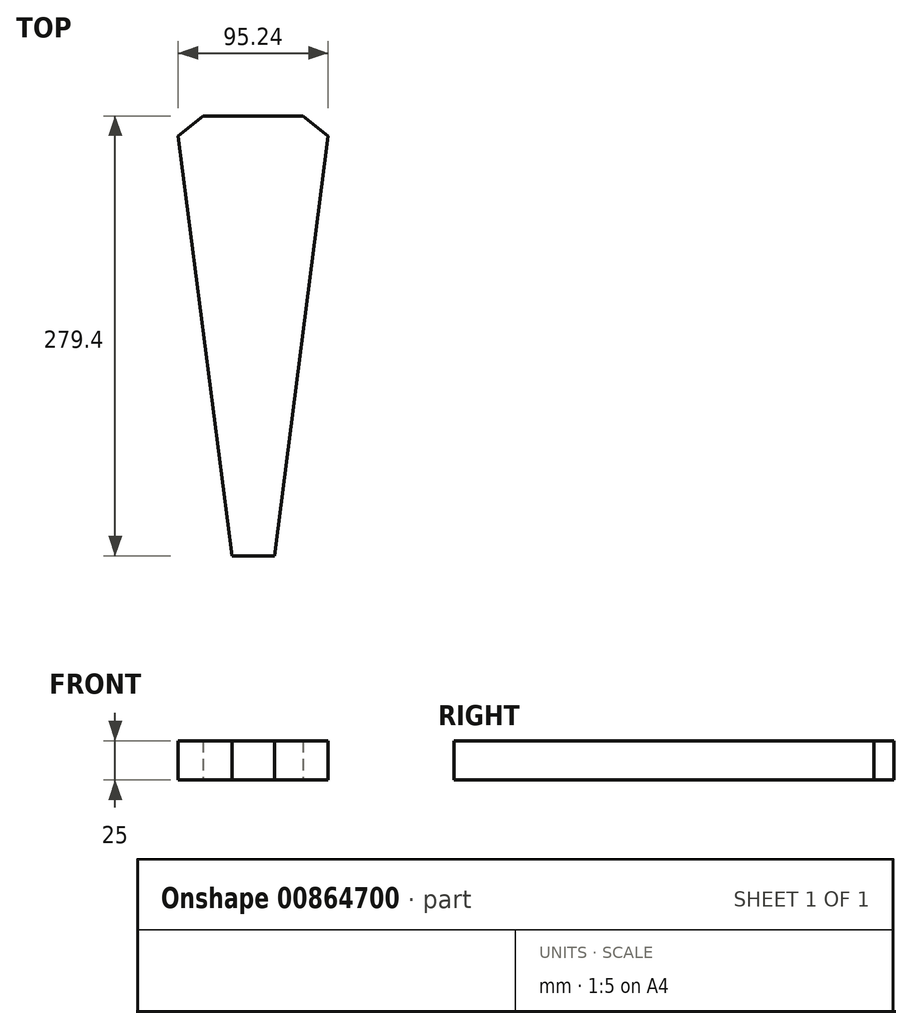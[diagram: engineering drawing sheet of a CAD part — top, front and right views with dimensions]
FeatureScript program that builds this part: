
annotation { "Feature Type Name" : "Feature", "Feature Type Description" : "" }
export const myFeature = defineFeature(function(context is Context, id is Id, definition is map)
    precondition{}
    {
        {
            var Q0;
            Q0=qCreatedBy(makeId("Top.planeOp"),FACE);
            var sketch = newSketch(context, id + "F0", { "sketchPlane" : qUnion([Q0])});
            skLineSegment(sketch, "E0.bottom", {"start": v(47.63, 139.7) * mm, "end": v(-47.62, 139.7) * mm, "construction": true});
            skLineSegment(sketch, "E0.top", {"start": v(47.62, -139.7) * mm, "end": v(-47.63, -139.7) * mm, "construction": true});
            skLineSegment(sketch, "E0.left", {"start": v(47.63, 139.7) * mm, "end": v(47.62, -139.7) * mm, "construction": true});
            skLineSegment(sketch, "E0.right", {"start": v(-47.62, 139.7) * mm, "end": v(-47.63, -139.7) * mm, "construction": true});
            skPoint(sketch, "E0.middle", {"position": v(0, 0) * mm});
            skLineSegment(sketch, "E1.bottom", {"start": v(13.5, 139.7) * mm, "end": v(-13.5, 139.7) * mm, "construction": true});
            skLineSegment(sketch, "E1.top", {"start": v(13.5, -139.7) * mm, "end": v(-13.5, -139.7) * mm, "construction": true});
            skLineSegment(sketch, "E1.left", {"start": v(13.5, 139.7) * mm, "end": v(13.5, -139.7) * mm, "construction": true});
            skLineSegment(sketch, "E1.right", {"start": v(-13.5, 139.7) * mm, "end": v(-13.5, -139.7) * mm, "construction": true});
            skLineSegment(sketch, "E2", {"start": v(47.62, 127) * mm, "end": v(-47.63, 127) * mm, "construction": true});
            skLineSegment(sketch, "E3", {"start": v(47.62, 127) * mm, "end": v(31.75, 139.7) * mm});
            skLineSegment(sketch, "E4", {"start": v(-47.63, 127) * mm, "end": v(-31.75, 139.7) * mm});
            skLineSegment(sketch, "E5", {"start": v(47.62, 127) * mm, "end": v(13.5, -139.7) * mm});
            skLineSegment(sketch, "E6", {"start": v(-47.63, 127) * mm, "end": v(-13.5, -139.7) * mm});
            skLineSegment(sketch, "E7", {"start": v(31.75, 139.7) * mm, "end": v(-31.75, 139.7) * mm});
            skLineSegment(sketch, "E8", {"start": v(13.5, -139.7) * mm, "end": v(-13.5, -139.7) * mm});
            skSolve(sketch);
        }
        {
            var Q0;
            Q0=makeQuery(id+"F0.imprint","IMPRINT",FACE,{"disambiguationData":[TD([[makeQuery(id+"F0.imprint","IMPRINT",EDGE,{"derivedFrom":sQuery(id+"F0.wireOp",EDGE,"E3")}),1.0]])]});
            extrude(context, id + "F1", {"entities" : qUnion([Q0]), "depth" : 25 * mm, "offsetDistance" : 25 * mm});
        }
    });
